# Revit family: LED DOWNLIGHT 01_LZ1541WW.20
name_source: partatom
category: Luminarias
units: mm (PartAtom-declared; Revit-internal decimal feet)

## family parameters
Compartido = No
Corte con vacíos al cargar = No
Cota de conector redondo = Diámetro de uso
Origen de luz = Sí
Punto de cálculo de habitación = No
Se basa en plano de trabajo = Sí
Siempre vertical = Sí
Tipo de pieza = Normal

## types (1)
- DWN_LZ1541WW.20
    Archivo de red fotométrica = LZ1541WW.IES
    Cambio de temperatura de color de luz atenuada = <Ninguno>
    Comentarios de vataje = 100-240-277V *se requeire accesorio
    Descripción = LUMINARIA TIPO CIRCULAR PARA EMPOTRAR EN TECHO CON CUERPO DE ALUMINIO ACABADO ANONIZADO, IP 20 USO PARA INTERIORES CON CUERPO DE 0.2KG, CUENTA CON 1 LED TIPO CREE CON UNA POTENCIA TOTAL DE 4W, A UNA TEMPERATURA EN BLANCO CALIDO 3000K CON 144LUMENES, EFICIENCIA DE 36LM/W, IRC 80, APERTURA A 20 GRADOS EN STOCK, 700mA EN CORRIENTE DE OPERACIÓN. SE REQUIEREN ACCESORIOS.
    Elevación por defecto = 1219 mm
    Fabricante = BRILLANT
    Filtro de color = 16777215
    Lámpara = CREE
    Modelo = LZ1541WW.20
    Watt per fixture = 4
    Ángulo de inclinación = 60.00°

## geometry (parser evidence)
native form markers: Blend x2
no freeform markers — native parametric forms only
